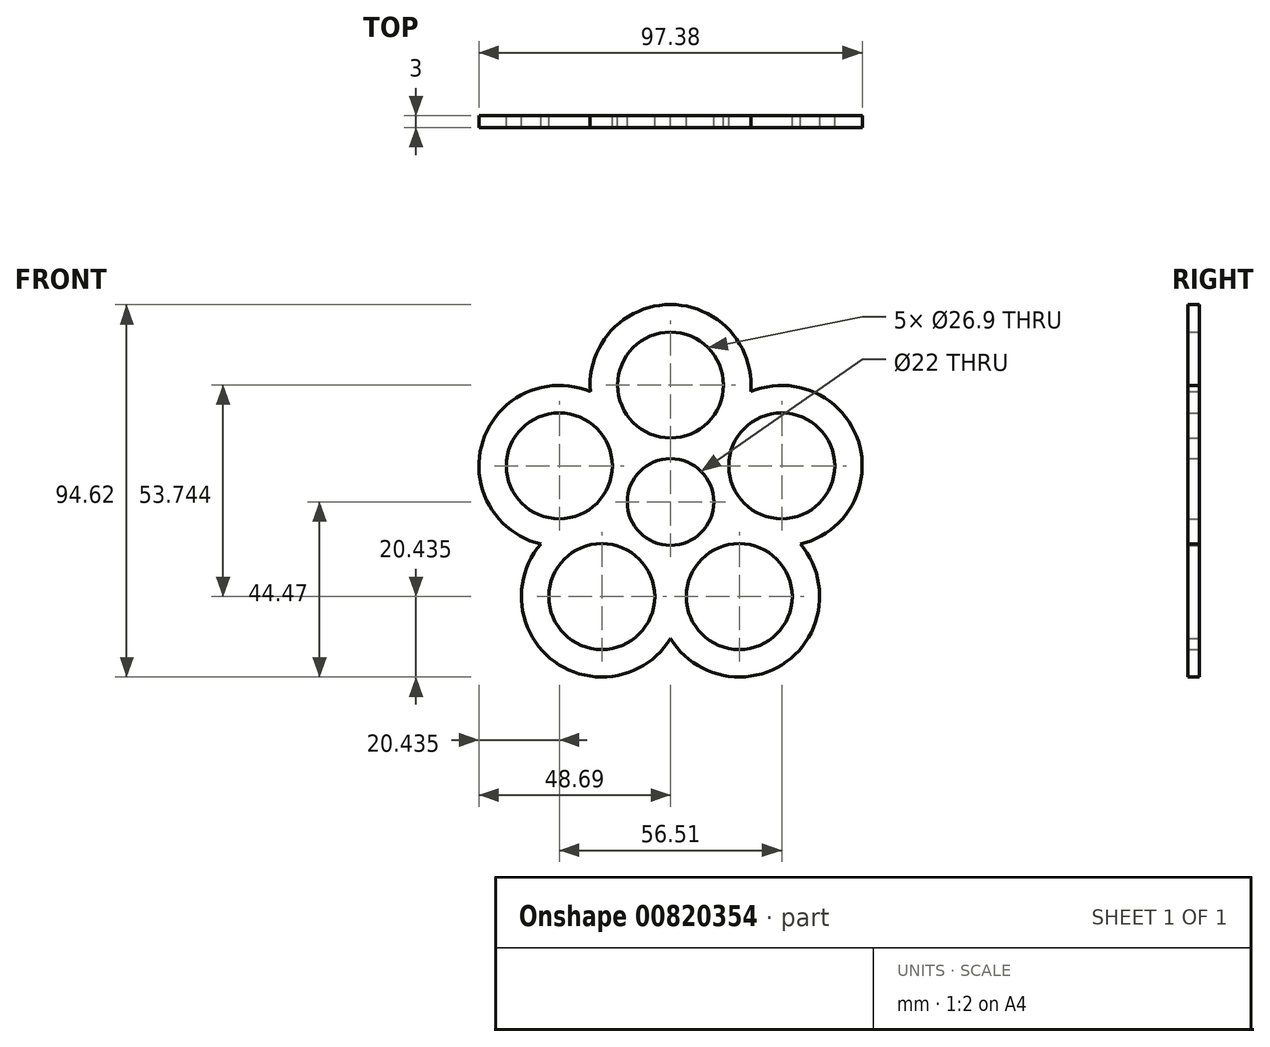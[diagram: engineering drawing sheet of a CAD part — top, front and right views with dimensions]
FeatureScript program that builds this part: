
annotation { "Feature Type Name" : "Feature", "Feature Type Description" : "" }
export const myFeature = defineFeature(function(context is Context, id is Id, definition is map)
    precondition{}
    {
        {
            var Q0;
            Q0=qCreatedBy(makeId("Front.planeOp"),FACE);
            var sketch = newSketch(context, id + "F0", { "sketchPlane" : qUnion([Q0])});
            skCircle(sketch, "E0", {"center": v(0, 0) * mm, "radius": 11 * mm});
            skCircle(sketch, "E1", {"center": v(0, 29.7) * mm, "radius": 13.45 * mm});
            skArc(sketch, "E2", {"start": v(20.37, 28.04) * mm, "mid": v(0, 50.15) * mm, "end": v(-20.37, 28.04) * mm});
            skArc(sketch, "E3.1.0", {"start": v(-20.37, 28.04) * mm, "mid": v(-47.7, 15.5) * mm, "end": v(-32.96, -10.7) * mm});
            skCircle(sketch, "E3.1.4", {"center": v(-28.25, 9.18) * mm, "radius": 13.45 * mm});
            skArc(sketch, "E3.2.0", {"start": v(-32.96, -10.7) * mm, "mid": v(-29.48, -40.57) * mm, "end": v(0, -34.66) * mm});
            skArc(sketch, "E3.2.2", {"start": v(-6.47, -8.9) * mm, "mid": v(10.96, -0.93) * mm, "end": v(-4.88, 9.86) * mm});
            skCircle(sketch, "E3.2.4", {"center": v(-17.46, -24.03) * mm, "radius": 13.45 * mm});
            skArc(sketch, "E3.3.0", {"start": v(0, -34.66) * mm, "mid": v(29.48, -40.57) * mm, "end": v(32.96, -10.7) * mm});
            skCircle(sketch, "E3.3.4", {"center": v(17.46, -24.03) * mm, "radius": 13.45 * mm});
            skCircle(sketch, "E3.4.4", {"center": v(28.25, 9.18) * mm, "radius": 13.45 * mm});
            skArc(sketch, "E4.trimOffspring", {"start": v(32.96, -10.7) * mm, "mid": v(47.7, 15.5) * mm, "end": v(20.37, 28.04) * mm});
            skArc(sketch, "E5.trimOffspring", {"start": v(-10.46, 3.4) * mm, "mid": v(-10.96, -0.93) * mm, "end": v(-9.74, -5.11) * mm});
            skSolve(sketch);
        }
        {
            var Q0;
            Q0 = qSketchRegion(id + "F0", true);
            extrude(context, id + "F1", {"entities" : qUnion([Q0]), "depth" : 3 * mm, "offsetDistance" : 25 * mm});
        }
    });
